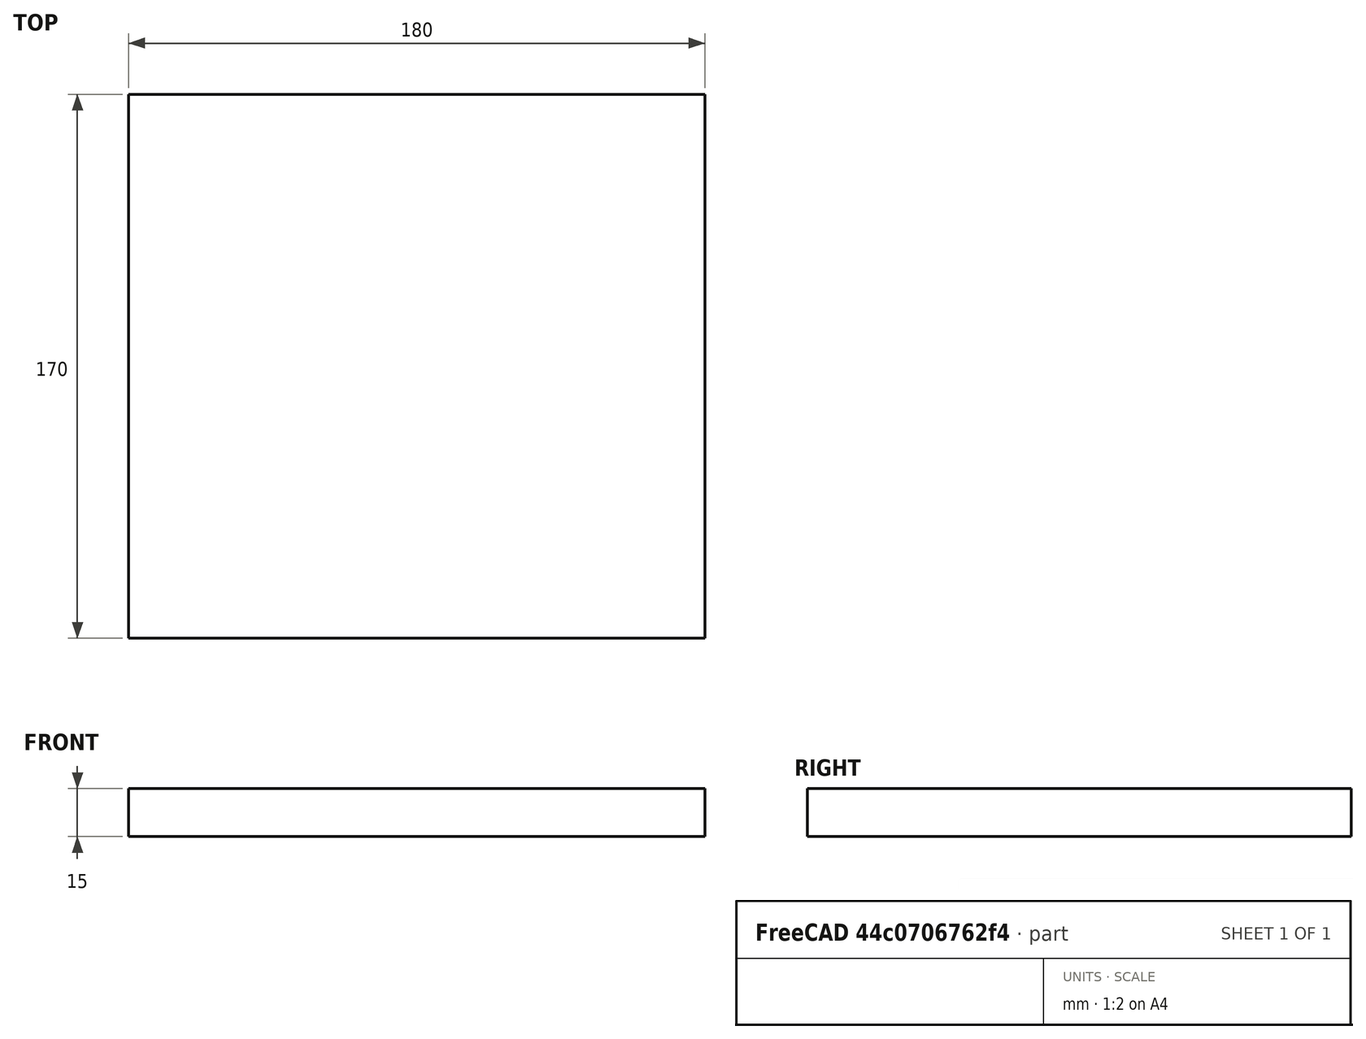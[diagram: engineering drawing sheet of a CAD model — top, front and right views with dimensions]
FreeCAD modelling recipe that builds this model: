
FCSTD DOCUMENT  (FreeCAD 0.18R4 (GitTag))
Label: MidBaseMedium-B
License: All rights reserved
LicenseURL: http://en.wikipedia.org/wiki/All_rights_reserved
objects: Sketcher::SketchObject×1, PartDesign::Pad×1, PartDesign::Body×1
note: 4 computed .brp shape members not serialized (recipe doc carries the construction recipe); baked Part::Feature solids carry a one-line shape summary decoded from their .brp

FEATURE [Sketcher::SketchObject] Sketch
  MapMode = 5
  Support = -> [XY_Plane]
  sketch-geometry (4):
    g0: LineSegment StartX=0 StartY=0 StartZ=0 EndX=-180 EndY=0 EndZ=0
    g1: LineSegment StartX=-180 StartY=0 StartZ=0 EndX=-180 EndY=170 EndZ=0
    g2: LineSegment StartX=-180 StartY=170 StartZ=0 EndX=0 EndY=170 EndZ=0
    g3: LineSegment StartX=0 StartY=170 StartZ=0 EndX=0 EndY=0 EndZ=0
  constraints (11):
    c: Coincident(g0,g1)
    c: Coincident(g1,g2)
    c: Coincident(g2,g3)
    c: Coincident(g3,g0)
    c: Horizontal(g0)
    c: Horizontal(g2)
    c: Vertical(g1)
    c: Vertical(g3)
    c: Distance(g2) = 180
    c: Distance(g3) = 170
    c: Coincident(g0,g-1)
FEATURE [PartDesign::Pad] Pad
  Length = 15
  Length2 = 100
  Profile = -> Sketch
  Type = 0
FEATURE [PartDesign::Body] Body
  Group = -> [Sketch,Pad]
  Origin = -> Origin
  Tip = -> Pad
